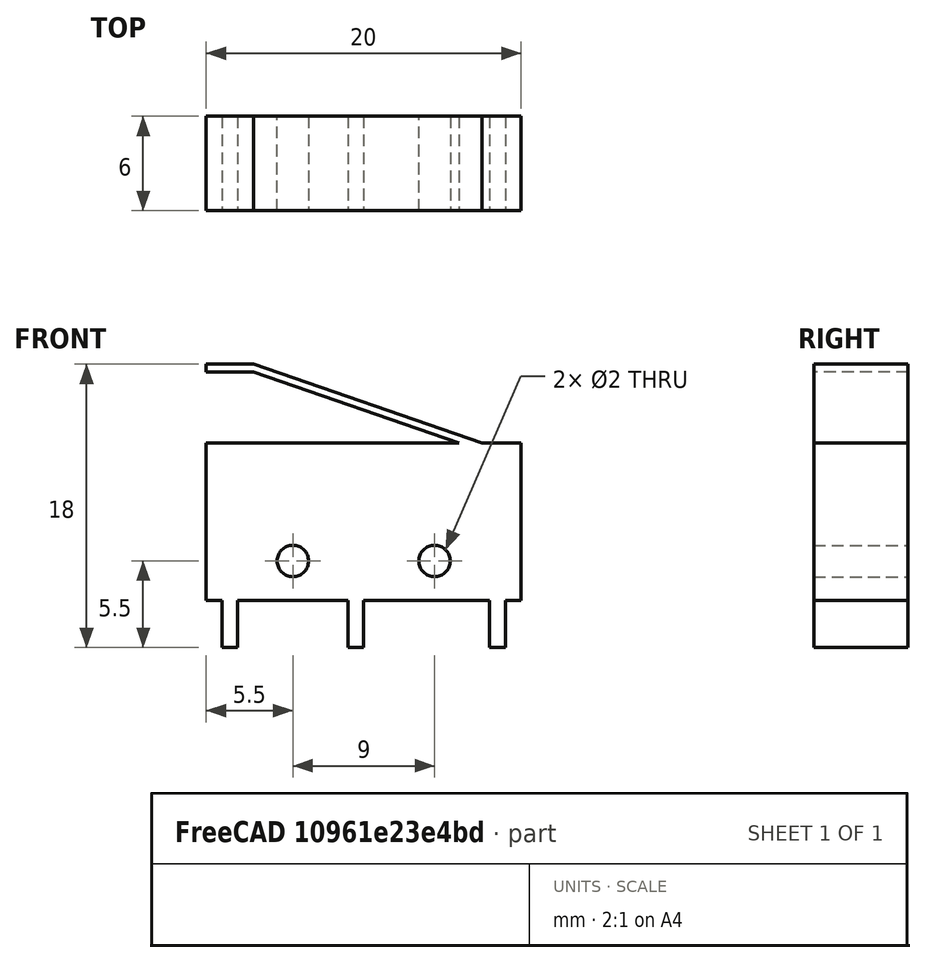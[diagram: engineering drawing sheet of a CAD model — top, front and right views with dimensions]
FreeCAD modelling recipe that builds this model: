
FCSTD DOCUMENT  (FreeCAD 0.18R14555 (Git shallow))
Label: endstop
License: All rights reserved
LicenseURL: http://en.wikipedia.org/wiki/All_rights_reserved
objects: Sketcher::SketchObject×1, PartDesign::Pad×1, PartDesign::Body×1
note: 4 computed .brp shape members not serialized (recipe doc carries the construction recipe); baked Part::Feature solids carry a one-line shape summary decoded from their .brp

FEATURE [Sketcher::SketchObject] Sketch
  MapMode = 5
  Placement = pos=(0,0,0) rot=(1,0,0;1.5708rad)
  Support = -> [XZ_Plane]
  sketch-geometry (37):
    g0: LineSegment StartX=0 StartY=13 StartZ=0 EndX=0 EndY=3 EndZ=0
    g1: LineSegment StartX=0 StartY=3 StartZ=0 EndX=1 EndY=3 EndZ=0
    g2: LineSegment StartX=1 StartY=3 StartZ=0 EndX=1 EndY=0 EndZ=0
    g3: LineSegment StartX=1 StartY=0 StartZ=0 EndX=2 EndY=0 EndZ=0
    g4: LineSegment StartX=2 StartY=0 StartZ=0 EndX=2 EndY=3 EndZ=0
    g5: LineSegment StartX=2 StartY=3 StartZ=0 EndX=9 EndY=3 EndZ=0
    g6: LineSegment StartX=9 StartY=3 StartZ=0 EndX=9 EndY=0 EndZ=0
    g7: LineSegment StartX=9 StartY=0 StartZ=0 EndX=10 EndY=0 EndZ=0
    g8: LineSegment StartX=10 StartY=0 StartZ=0 EndX=10 EndY=3 EndZ=0
    g9: LineSegment StartX=10 StartY=3 StartZ=0 EndX=18 EndY=3 EndZ=0
    g10: LineSegment StartX=18 StartY=3 StartZ=0 EndX=18 EndY=0 EndZ=0
    g11: LineSegment StartX=18 StartY=0 StartZ=0 EndX=19 EndY=0 EndZ=0
    g12: LineSegment StartX=19 StartY=0 StartZ=0 EndX=19 EndY=3 EndZ=0
    g13: LineSegment StartX=19 StartY=3 StartZ=0 EndX=20 EndY=3 EndZ=0
    g14: LineSegment StartX=20 StartY=3 StartZ=0 EndX=20 EndY=13 EndZ=0
    g15: LineSegment StartX=20 StartY=13 StartZ=0 EndX=17.5 EndY=13 EndZ=0
    g16: LineSegment StartX=17.5 StartY=13 StartZ=0 EndX=3 EndY=18 EndZ=0
    g17: LineSegment StartX=3 StartY=18 StartZ=0 EndX=0 EndY=18 EndZ=0
    g18: LineSegment StartX=0 StartY=18 StartZ=0 EndX=0 EndY=17.5 EndZ=0
    g19: LineSegment StartX=0 StartY=17.5 StartZ=0 EndX=3 EndY=17.5 EndZ=0
    g20: LineSegment StartX=3 StartY=17.5 StartZ=0 EndX=16.05 EndY=13 EndZ=0
    g21: LineSegment StartX=16.05 StartY=13 StartZ=0 EndX=0 EndY=13 EndZ=0
    g22: LineSegment [constr] StartX=2 StartY=0 StartZ=0 EndX=9 EndY=0 EndZ=0
    g23: LineSegment [constr] StartX=10 StartY=0 StartZ=0 EndX=18 EndY=0 EndZ=0
    g24: LineSegment [constr] StartX=1 StartY=3 StartZ=0 EndX=2 EndY=3 EndZ=0
    g25: LineSegment [constr] StartX=9 StartY=3 StartZ=0 EndX=10 EndY=3 EndZ=0
    g26: LineSegment [constr] StartX=18 StartY=3 StartZ=0 EndX=19 EndY=3 EndZ=0
    g27: LineSegment [constr] StartX=16.05 StartY=13 StartZ=0 EndX=17.5 EndY=13 EndZ=0
    g28: LineSegment [constr] StartX=3 StartY=17.5 StartZ=0 EndX=3 EndY=18 EndZ=0
    g29: LineSegment [constr] StartX=0 StartY=13 StartZ=0 EndX=0 EndY=17.5 EndZ=0
    g30: LineSegment [constr] StartX=0 StartY=3 StartZ=0 EndX=0 EndY=0 EndZ=0
    g31: LineSegment [constr] StartX=0 StartY=0 StartZ=0 EndX=1 EndY=0 EndZ=0
    g32: Circle CenterX=5.5 CenterY=5.5 CenterZ=0 NormalX=0 NormalY=0 NormalZ=1 AngleXU=0 Radius=1
    g33: Circle CenterX=14.5 CenterY=5.5 CenterZ=0 NormalX=0 NormalY=0 NormalZ=1 AngleXU=0 Radius=1
    g34: LineSegment [constr] StartX=0 StartY=5.5 StartZ=0 EndX=5.5 EndY=5.5 EndZ=0
    g35: LineSegment [constr] StartX=5.5 StartY=5.5 StartZ=0 EndX=14.5 EndY=5.5 EndZ=0
    g36: LineSegment [constr] StartX=14.5 StartY=5.5 StartZ=0 EndX=20 EndY=5.5 EndZ=0
  constraints (100):
    c: Vertical(g0)
    c: Coincident(g0,g1)
    c: Horizontal(g1)
    c: Coincident(g1,g2)
    c: Vertical(g2)
    c: Coincident(g2,g3)
    c: Horizontal(g3)
    c: Coincident(g3,g4)
    c: Vertical(g4)
    c: Coincident(g4,g5)
    c: Horizontal(g5)
    c: Coincident(g5,g6)
    c: Vertical(g6)
    c: Coincident(g6,g7)
    c: Horizontal(g7)
    c: Coincident(g7,g8)
    c: Vertical(g8)
    c: Coincident(g8,g9)
    c: Coincident(g9,g10)
    c: Vertical(g10)
    c: Coincident(g10,g11)
    c: Coincident(g11,g12)
    c: Vertical(g12)
    c: Coincident(g12,g13)
    c: Coincident(g13,g14)
    c: Vertical(g14)
    c: Coincident(g14,g15)
    c: Horizontal(g15)
    c: Coincident(g15,g16)
    c: Coincident(g16,g17)
    c: Horizontal(g17)
    c: Coincident(g17,g18)
    c: Vertical(g18)
    c: Coincident(g18,g19)
    c: Coincident(g19,g20)
    c: Coincident(g20,g21)
    c: Horizontal(g21)
    c: Coincident(g0,g21)
    c: Parallel(g20,g16)
    c: Horizontal(g9)
    c: Horizontal(g11)
    c: Horizontal(g19)
    c: Coincident(g22,g3)
    c: Coincident(g22,g6)
    c: Coincident(g23,g7)
    c: Coincident(g23,g10)
    c: Horizontal(g23)
    c: Horizontal(g22)
    c: Horizontal(g13)
    c: Coincident(g24,g1)
    c: Coincident(g24,g4)
    c: Coincident(g25,g5)
    c: Coincident(g25,g8)
    c: Coincident(g26,g9)
    c: Horizontal(g26)
    c: Coincident(g26,g12)
    c: Horizontal(g25)
    c: Horizontal(g24)
    c: DistanceX(g0,g13) = 20
    c: DistanceY(g2,g1) = 3
    c: DistanceX(g0,g1) = 1
    c: DistanceX(g3,g3) = 1
    c: DistanceX(g5,g5) = 7
    c: Equal(g3,g7)
    c: Equal(g7,g11)
    c: DistanceX(g8,g9) = 8
    c: DistanceY(g14,g14) = 10
    c: Coincident(g27,g20)
    c: Coincident(g27,g15)
    c: Horizontal(g27)
    c: DistanceY(g18,g18) = 0.5
    c: Coincident(g28,g19)
    c: Coincident(g28,g16)
    c: Vertical(g28)
    c: Coincident(g29,g0)
    c: Coincident(g29,g18)
    c: Vertical(g29)
    c: DistanceY(g0,g17) = 5
    c: DistanceX(g15,g15) = 2.5
    c: DistanceX(g17,g17) = 3
    c: Coincident(g30,g0)
    c: Vertical(g30)
    c: Coincident(g31,g30)
    c: Coincident(g31,g2)
    c: Horizontal(g31)
    c: Coincident(g30,g-1)
    c: PointOnObject(g34,g0)
    c: Horizontal(g34)
    c: Coincident(g35,g32)
    c: Coincident(g35,g33)
    c: Horizontal(g35)
    c: PointOnObject(g36,g14)
    c: Horizontal(g36)
    c: Equal(g36,g34)
    c: Coincident(g34,g32)
    c: Equal(g33,g32)
    c: Radius(g32) = 1
    c: Coincident(g36,g33)
    c: DistanceX(g35,g35) = 9
    c: DistanceY(g0,g32) = 2.5
FEATURE [PartDesign::Pad] Pad
  Length = 6
  Length2 = 100
  Placement = pos=(0,0,0) rot=(1,0,0;1.5708rad)
  Profile = -> Sketch
  Type = 0
FEATURE [PartDesign::Body] Body
  Group = -> [Sketch,Pad]
  Origin = -> Origin
  Tip = -> Pad
